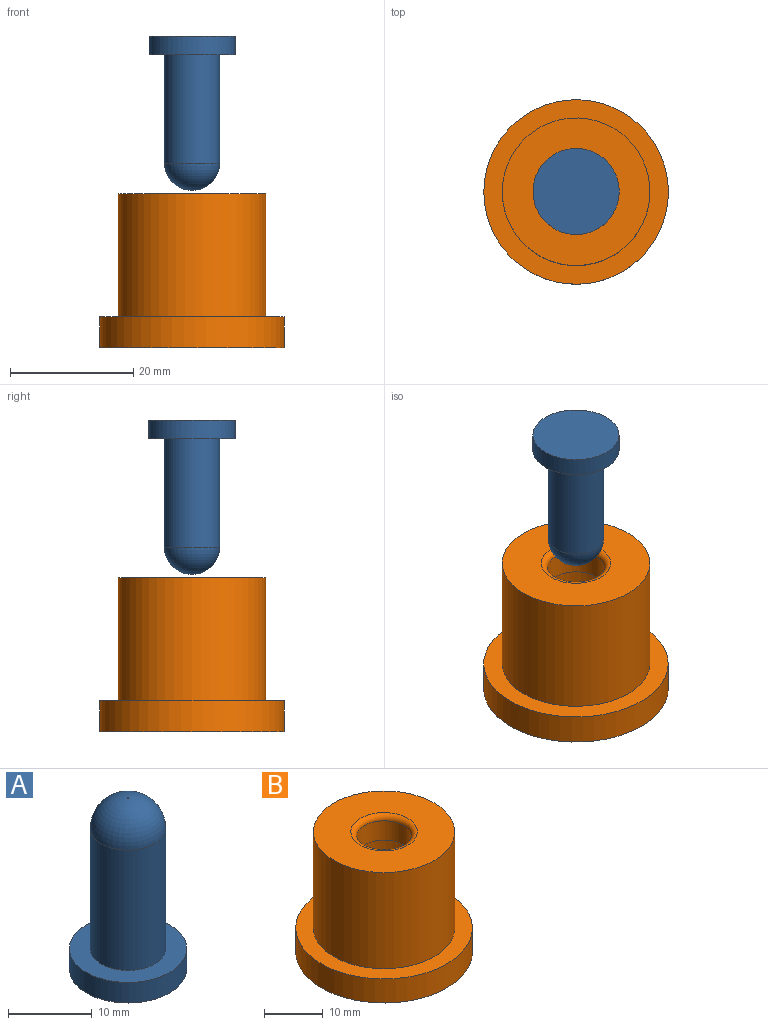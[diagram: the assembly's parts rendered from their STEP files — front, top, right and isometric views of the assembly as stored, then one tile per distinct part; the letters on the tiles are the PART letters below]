
ASSEMBLY  parts=2 mates=2
PART A: 6 faces, bbox 14x14x25 mm
  f0: cylinder r=4.5mm len=17.57mm, axis (0,0,-1), area 496.8mm2, adj f2,f4
  f1: plane 0.14x0.14mm, normal (0,0,1), area 0mm2, adj f2
  f2: torus R=0.07mm, axis (0,0,1), area 126.4mm2, adj f0,f1
  f3: cylinder r=7mm len=14mm, axis (0,0,-1), area 131.9mm2, adj f4,f5
  f4: plane 14x14mm, normal (0,0,1), area 90.3mm2, adj f0,f3
  f5: plane 14x14mm, normal (0,0,-1), area 153.9mm2, adj f3
PART B: 9 faces, bbox 30x30x25 mm
  f0: cylinder r=15mm len=30mm, axis (0,0,-1), area 471.2mm2, adj f1,f2
  f1: plane 30x30mm, normal (0,0,1), area 254.5mm2, adj f0,f3
  f2: plane 30x30mm, normal (0,0,-1), area 505.8mm2, adj f0,f8
  f3: cylinder r=12mm len=24mm, axis (0,0,-1), area 1508mm2, adj f1,f5
  f4: cylinder r=4.64mm len=9.28mm, axis (0,0,-1), area 116.6mm2, adj f6,f7
  f5: plane 24x24mm, normal (0,0,1), area 352.5mm2, adj f3,f7
  f6: plane 16x16mm, normal (0,0,-1), area 133.4mm2, adj f4,f8
  f7: torus R=5.64mm, axis (0,0,1), area 49.4mm2, adj f4,f5
  f8: cylinder r=8mm len=20mm, axis (0,0,-1), area 1005.3mm2, adj f2,f6
PLACE A rot(axis=(0,-1,0),180deg) t=(-12.75,-18.45,13.72)mm
PLACE B rot(axis=(0,0,-1),180deg) t=(-12.75,-18.45,-11.85)mm
MATE slider A.f0 <-> B.f4  axis (0,0,-1) through (-12.75,-18.45,15.02)mm
MATE slider A.f0 <-> B.f4  axis (0,0,1) through (-12.75,-18.45,18.15)mm
